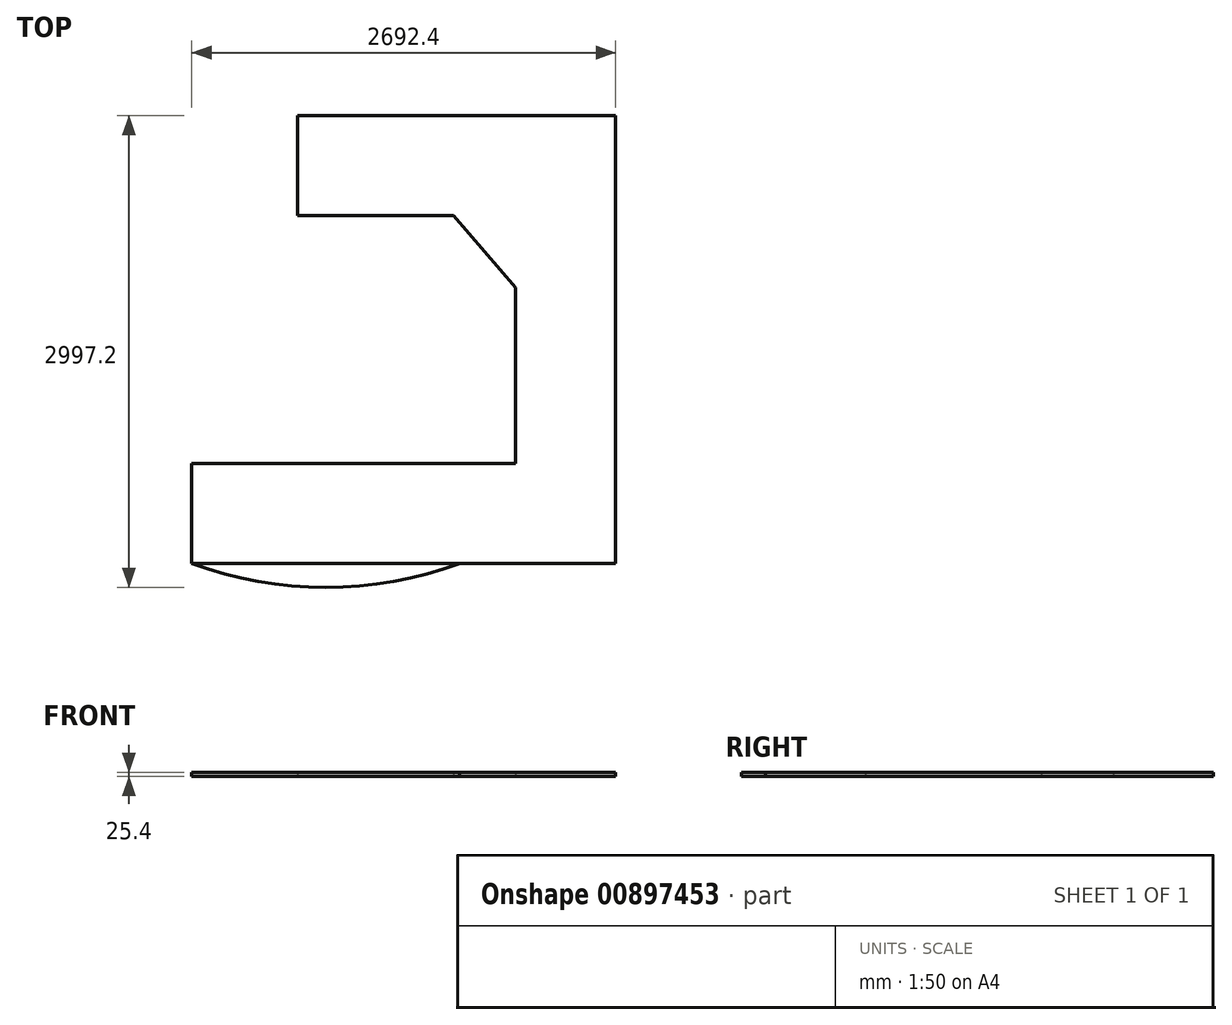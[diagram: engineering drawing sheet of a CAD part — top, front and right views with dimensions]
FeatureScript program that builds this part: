
annotation { "Feature Type Name" : "Feature", "Feature Type Description" : "" }
export const myFeature = defineFeature(function(context is Context, id is Id, definition is map)
    precondition{}
    {
        {
            var Q0;
            Q0=qCreatedBy(makeId("Top.planeOp"),FACE);
            var sketch = newSketch(context, id + "F0", { "sketchPlane" : qUnion([Q0])});
            skLineSegment(sketch, "E0", {"start": v(-1384.3, 635) * mm, "end": v(635, 635) * mm});
            skLineSegment(sketch, "E1", {"start": v(635, 635) * mm, "end": v(635, -2209.8) * mm});
            skLineSegment(sketch, "E2", {"start": v(-1384.3, 635) * mm, "end": v(-1384.3, 0) * mm});
            skLineSegment(sketch, "E3", {"start": v(-1384.3, 0) * mm, "end": v(-393.7, 0) * mm});
            skLineSegment(sketch, "E4", {"start": v(-393.7, 0) * mm, "end": v(0, -457.2) * mm});
            skLineSegment(sketch, "E5", {"start": v(0, -457.2) * mm, "end": v(0, -1574.8) * mm});
            skLineSegment(sketch, "E6", {"start": v(0, -1574.8) * mm, "end": v(-2057.4, -1574.8) * mm});
            skLineSegment(sketch, "E7", {"start": v(-2057.4, -1574.8) * mm, "end": v(-2057.4, -2209.8) * mm});
            skLineSegment(sketch, "E8", {"start": v(-2057.4, -2209.8) * mm, "end": v(635, -2209.8) * mm});
            skSolve(sketch);
        }
        {
            var Q0;
            Q0 = qSketchRegion(id + "F0", true);
            extrude(context, id + "F1", {"entities" : qUnion([Q0]), "depth" : 25.4 * mm, "offsetDistance" : 25.4 * mm});
        }
        {
            var Q0;
            Q0=makeQuery(id+"F1.opExtrude","CAP_FACE",FACE,{"disambiguationData":[OSD([sQuery(id+"F0.wireOp",EDGE,"E0"),sQuery(id+"F0.wireOp",EDGE,"E1"),sQuery(id+"F0.wireOp",EDGE,"E2"),sQuery(id+"F0.wireOp",EDGE,"E3"),sQuery(id+"F0.wireOp",EDGE,"E4"),sQuery(id+"F0.wireOp",EDGE,"E5"),sQuery(id+"F0.wireOp",EDGE,"E6"),sQuery(id+"F0.wireOp",EDGE,"E7"),sQuery(id+"F0.wireOp",EDGE,"E8")])],"isStart":false});
            var sketch = newSketch(context, id + "F2", { "sketchPlane" : qUnion([Q0])});
            skArc(sketch, "E9", {"start": v(-2057.4, -2209.8) * mm, "mid": v(-1206.5, -2362.2) * mm, "end": v(-355.6, -2209.8) * mm});
            skLineSegment(sketch, "E10", {"start": v(-2057.4, -2209.8) * mm, "end": v(-355.6, -2209.8) * mm});
            skSolve(sketch);
        }
        {
            var Q0;
            Q0 = qSketchRegion(id + "F2", true);
            extrude(context, id + "F3", {"entities" : qUnion([Q0]), "oppositeDirection" : true, "depth" : 25.4 * mm, "offsetDistance" : 25.4 * mm});
        }
    });
